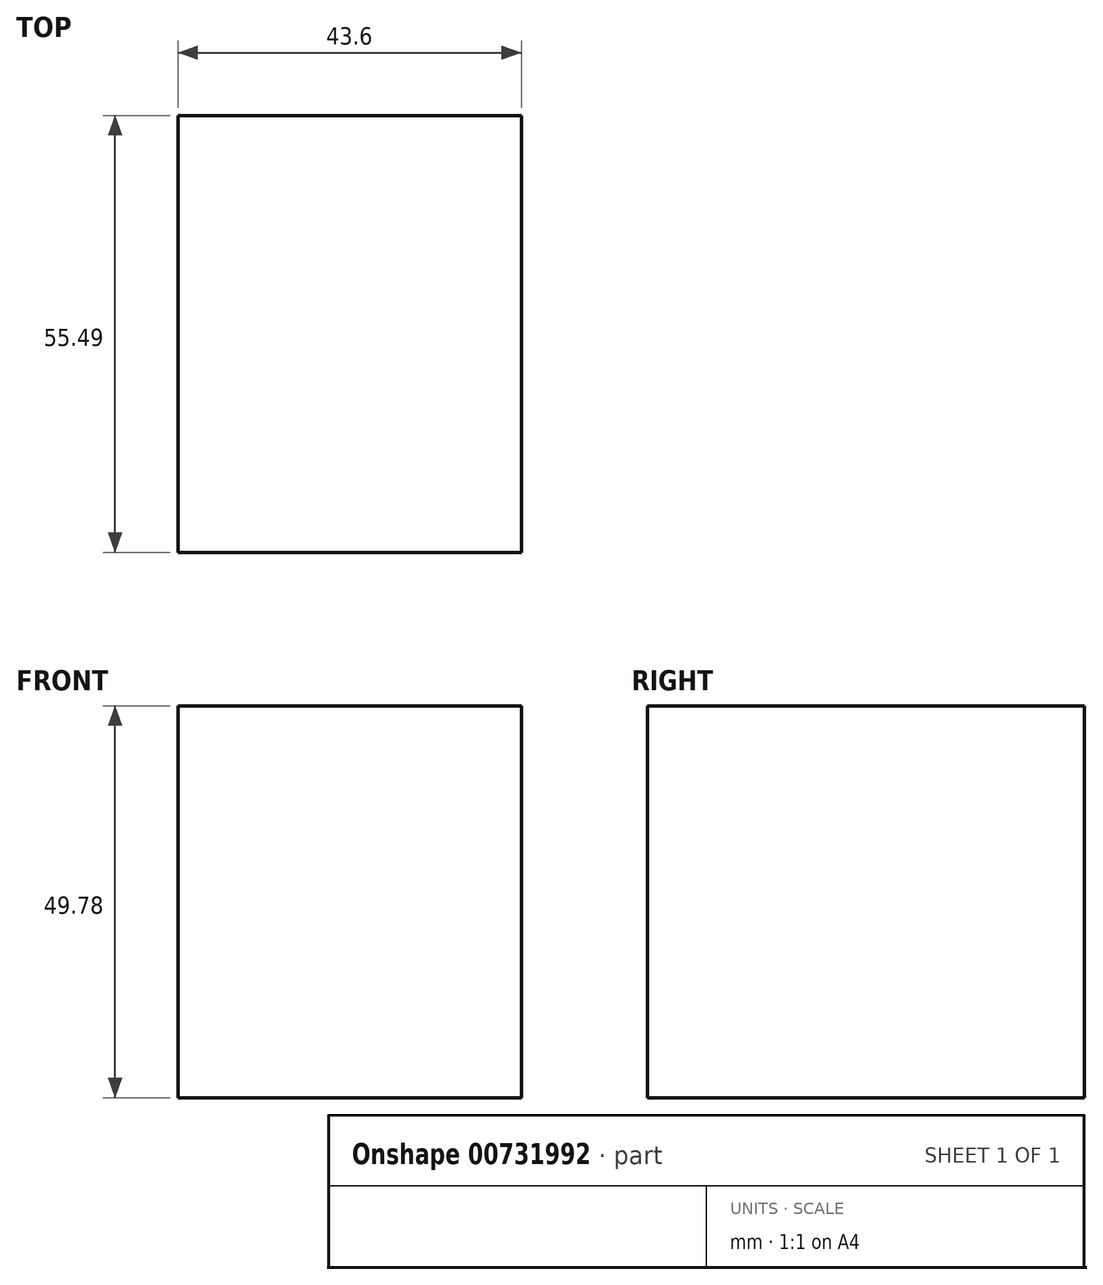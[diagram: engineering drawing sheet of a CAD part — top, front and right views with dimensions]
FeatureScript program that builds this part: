
annotation { "Feature Type Name" : "Feature", "Feature Type Description" : "" }
export const myFeature = defineFeature(function(context is Context, id is Id, definition is map)
    precondition{}
    {
        {
            var Q0;
            Q0=qCreatedBy(makeId("Top.planeOp"),FACE);
            var sketch = newSketch(context, id + "F0", { "sketchPlane" : qUnion([Q0])});
            skLineSegment(sketch, "E0.bottom", {"start": v(-43.6, 0) * mm, "end": v(0, 0) * mm});
            skLineSegment(sketch, "E0.top", {"start": v(-43.6, 55.5) * mm, "end": v(0, 55.5) * mm});
            skLineSegment(sketch, "E0.left", {"start": v(-43.6, 0) * mm, "end": v(-43.6, 55.5) * mm});
            skLineSegment(sketch, "E0.right", {"start": v(0, 0) * mm, "end": v(0, 55.5) * mm});
            skSolve(sketch);
        }
        {
            var Q0;
            Q0=makeQuery(id+"F0.imprint","IMPRINT",FACE,{"disambiguationData":[TD([[makeQuery(id+"F0.imprint","IMPRINT",EDGE,{"derivedFrom":sQuery(id+"F0.wireOp",EDGE,"E0.bottom")}),1.0]])]});
            extrude(context, id + "F1", {"entities" : qUnion([Q0]), "depth" : 49.78 * mm, "offsetDistance" : 25.4 * mm});
        }
    });
